# Revit family: FD-C
name_source: partatom
category: Mechanical Equipment
revit_build: Autodesk Revit 2015 (Build: 20140606_1530(x64)
units: mm (PartAtom-declared; Revit-internal decimal feet)

## types (1)
- FD-C
    Damper Height = 2' - 4"
    Depth = 0' - 3 11/16"
    Description = Curtain Fire Damper for use in Static Systems
    Diameter = 2' - 0"
    Exact Width = 2' - 1"
    Keynote = Round Transitions Shown, Consult Factory for Models with Rectangular, or Oval Transitions
    Manufacturer = United Enertech Corporation
    Model = FD-C
    Type Comments = Max. Sizes are (1-1/2 Hour Rect./Oval Vertical 119"w x 114"h) (1-1/2 Hour Rect./Oval Horizontal 119"w x 35"h or 95"w x 42"h) (1-1/2 Hour Round Vertical 48" Diameter) (1-1/2 Hour Round Horizontal 42" Diameter) (3 Hour Rect./Oval Vertical 79"w x 35"h) (3 Hour Rect./Oval Horizontal 79"w x 35"h) (3 Hour Round Vertical 36" Diameter) (3 Hour Round Horizontal 36" Diameter)
    URL = http://unitedenertech.com

## geometry (parser evidence)
native form markers: Sweep x20
no freeform markers — native parametric forms only
